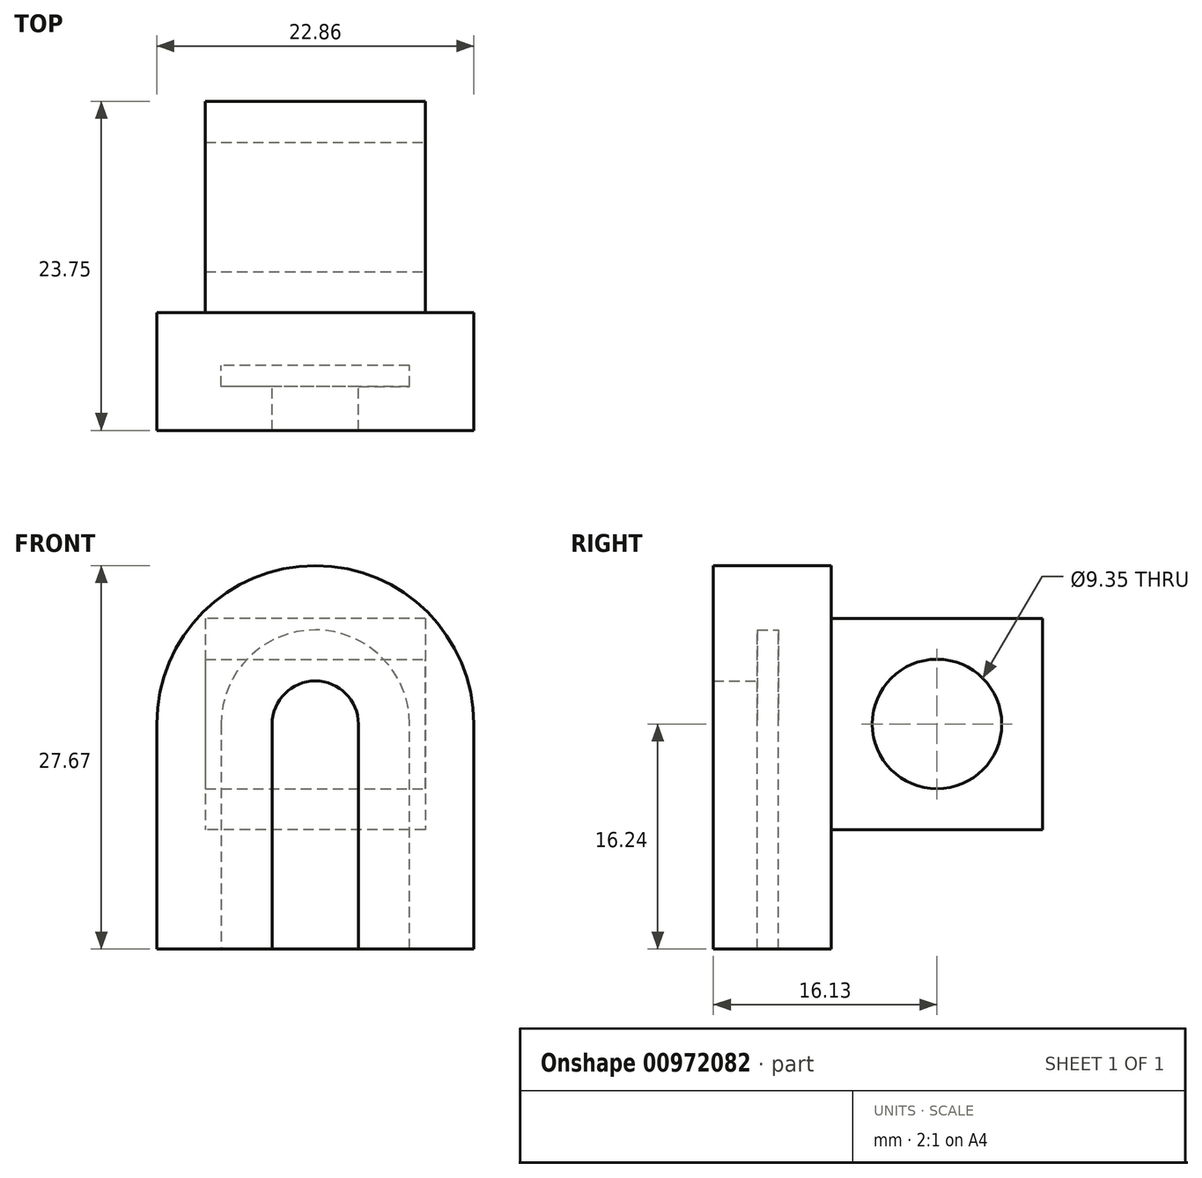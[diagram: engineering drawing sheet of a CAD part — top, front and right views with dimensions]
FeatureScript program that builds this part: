
annotation { "Feature Type Name" : "Feature", "Feature Type Description" : "" }
export const myFeature = defineFeature(function(context is Context, id is Id, definition is map)
    precondition{}
    {
        {
            var Q0;
            Q0=qCreatedBy(makeId("Front.planeOp"),FACE);
            var sketch = newSketch(context, id + "F0", { "sketchPlane" : qUnion([Q0])});
            skCircle(sketch, "E0", {"center": v(0, 0) * mm, "radius": 11.43 * mm});
            skPoint(sketch, "E1.middle", {"position": v(0, -11.43) * mm});
            skLineSegment(sketch, "E2.bottom", {"start": v(11.43, 0) * mm, "end": v(-11.43, 0) * mm});
            skLineSegment(sketch, "E2.top", {"start": v(11.43, -16.24) * mm, "end": v(-11.43, -16.24) * mm});
            skLineSegment(sketch, "E2.left", {"start": v(11.43, 0) * mm, "end": v(11.43, -16.24) * mm});
            skLineSegment(sketch, "E2.right", {"start": v(-11.43, 0) * mm, "end": v(-11.43, -16.24) * mm});
            skSolve(sketch);
        }
        {
            var Q0;
            Q0=qSketchRegion(id+"F0",true);
            extrude(context, id + "F1", {"entities" : qUnion([Q0]), "depth" : 3.8 * mm, "offsetDistance" : 25.4 * mm});
        }
        {
            var Q0;
            Q0=makeQuery(id+"F1.opExtrude","CAP_FACE",FACE,{"disambiguationData":[OSD([sQuery(id+"F0.wireOp",EDGE,"E0"),sQuery(id+"F0.wireOp",EDGE,"E2.top"),sQuery(id+"F0.wireOp",EDGE,"E2.left"),sQuery(id+"F0.wireOp",EDGE,"E2.right")])],"isStart":false});
            var sketch = newSketch(context, id + "F2", { "sketchPlane" : qUnion([Q0])});
            skArc(sketch, "E3.0", {"start": v(11.43, 0) * mm, "mid": v(0, 11.43) * mm, "end": v(-11.43, 0) * mm});
            skLineSegment(sketch, "E3.1", {"start": v(11.43, -16.24) * mm, "end": v(11.43, 0) * mm});
            skLineSegment(sketch, "E3.2", {"start": v(-11.43, -16.24) * mm, "end": v(11.43, -16.24) * mm});
            skLineSegment(sketch, "E3.3", {"start": v(-11.43, 0) * mm, "end": v(-11.43, -16.24) * mm});
            skArc(sketch, "E4.0", {"start": v(6.8, 0) * mm, "mid": v(0, 6.8) * mm, "end": v(-6.8, 0) * mm});
            skLineSegment(sketch, "E4.1", {"start": v(6.8, -11.6) * mm, "end": v(6.8, 0) * mm});
            skLineSegment(sketch, "E4.2", {"start": v(-6.8, -11.6) * mm, "end": v(6.8, -11.6) * mm});
            skLineSegment(sketch, "E4.3", {"start": v(-6.8, 0) * mm, "end": v(-6.8, -11.6) * mm});
            skLineSegment(sketch, "E5", {"start": v(-6.8, -11.6) * mm, "end": v(-6.8, -16.24) * mm});
            skLineSegment(sketch, "E6", {"start": v(6.8, -11.6) * mm, "end": v(6.8, -16.24) * mm});
            skSolve(sketch);
        }
        {
            var Q0;
            Q0=makeQuery(id+"F2.imprint","IMPRINT",FACE,{"disambiguationData":[TD([[makeQuery(id+"F2.imprint","IMPRINT",EDGE,{"derivedFrom":sQuery(id+"F2.wireOp",EDGE,"E3.0")}),1.0]])]});
            extrude(context, id + "F3", {"entities" : qUnion([Q0]), "operationType" : NewBodyOperationType.ADD, "depth" : 1.52 * mm, "offsetDistance" : 25.4 * mm});
        }
        {
            var Q0;
            Q0=makeQuery(id+"F3.opExtrude","CAP_FACE",FACE,{"disambiguationData":[OSD([sQuery(id+"F2.wireOp",EDGE,"E3.0"),sQuery(id+"F2.wireOp",EDGE,"E3.1"),sQuery(id+"F2.wireOp",EDGE,"E3.2"),sQuery(id+"F2.wireOp",EDGE,"E3.3"),sQuery(id+"F2.wireOp",EDGE,"E4.0"),sQuery(id+"F2.wireOp",EDGE,"E4.1"),sQuery(id+"F2.wireOp",EDGE,"E4.3"),sQuery(id+"F2.wireOp",EDGE,"E5"),sQuery(id+"F2.wireOp",EDGE,"E6")])],"isStart":false});
            var sketch = newSketch(context, id + "F4", { "sketchPlane" : qUnion([Q0])});
            skLineSegment(sketch, "E7.0", {"start": v(-3.11, 0) * mm, "end": v(-3.11, -16.24) * mm});
            skArc(sketch, "E7.1", {"start": v(3.11, 0) * mm, "mid": v(0, 3.11) * mm, "end": v(-3.11, 0) * mm});
            skLineSegment(sketch, "E7.2", {"start": v(3.11, 0) * mm, "end": v(3.11, -16.24) * mm});
            skLineSegment(sketch, "E8.0", {"start": v(-11.43, 0) * mm, "end": v(-11.43, -16.24) * mm});
            skArc(sketch, "E8.1", {"start": v(11.43, 0) * mm, "mid": v(0, 11.43) * mm, "end": v(-11.43, 0) * mm});
            skLineSegment(sketch, "E8.2", {"start": v(11.43, 0) * mm, "end": v(11.43, -16.24) * mm});
            skLineSegment(sketch, "E9", {"start": v(3.11, -16.24) * mm, "end": v(11.43, -16.24) * mm});
            skLineSegment(sketch, "E10", {"start": v(-3.11, -16.24) * mm, "end": v(-11.43, -16.24) * mm});
            skSolve(sketch);
        }
        {
            var Q0;
            Q0=qSketchRegion(id+"F4",true);
            extrude(context, id + "F5", {"entities" : qUnion([Q0]), "operationType" : NewBodyOperationType.ADD, "depth" : 3.17 * mm, "offsetDistance" : 25.4 * mm});
        }
        {
            var Q0;
            Q0=makeQuery(id+"F1.opExtrude","CAP_FACE",FACE,{"disambiguationData":[OSD([sQuery(id+"F0.wireOp",EDGE,"E0"),sQuery(id+"F0.wireOp",EDGE,"E2.top"),sQuery(id+"F0.wireOp",EDGE,"E2.left"),sQuery(id+"F0.wireOp",EDGE,"E2.right")])],"isStart":true});
            var sketch = newSketch(context, id + "F6", { "sketchPlane" : qUnion([Q0])});
            skLineSegment(sketch, "E11.bottom", {"start": v(-7.94, 7.62) * mm, "end": v(7.94, 7.62) * mm});
            skLineSegment(sketch, "E11.top", {"start": v(-7.94, -7.62) * mm, "end": v(7.94, -7.62) * mm});
            skLineSegment(sketch, "E11.left", {"start": v(-7.94, 7.62) * mm, "end": v(-7.94, -7.62) * mm});
            skLineSegment(sketch, "E11.right", {"start": v(7.94, 7.62) * mm, "end": v(7.94, -7.62) * mm});
            skPoint(sketch, "E11.middle", {"position": v(0, 0) * mm});
            skSolve(sketch);
        }
        {
            var Q0;
            Q0=qSketchRegion(id+"F6",true);
            extrude(context, id + "F7", {"entities" : qUnion([Q0]), "operationType" : NewBodyOperationType.ADD, "depth" : 15.24 * mm, "offsetDistance" : 25.4 * mm});
        }
        {
            var Q0;
            Q0=makeQuery(id+"F7.opExtrude","SWEPT_FACE",FACE,{"disambiguationData":[OSD([sQuery(id+"F6.wireOp",EDGE,"E11.left")])]});
            var sketch = newSketch(context, id + "F8", { "sketchPlane" : qUnion([Q0])});
            skCircle(sketch, "E12", {"center": v(7.62, 0) * mm, "radius": 4.67 * mm});
            skSolve(sketch);
        }
        {
            var Q0;
            Q0=qSketchRegion(id+"F8",true);
            extrude(context, id + "F9", {"entities" : qUnion([Q0]), "operationType" : NewBodyOperationType.REMOVE, "endBound" : BoundingType.THROUGH_ALL, "oppositeDirection" : true, "depth" : 25.4 * mm, "offsetDistance" : 25.4 * mm});
        }
    });
